FCSTD DOCUMENT
Label: gyuru_volume_alja_teljes
objects: Sketcher::SketchObject×1
note: 1 computed .brp shape members not serialized (recipe doc carries the construction recipe); baked Part::Feature solids carry a one-line shape summary decoded from their .brp

FEATURE [Sketcher::SketchObject] Sketch
  sketch-geometry (6):
    g0: LineSegment [constr] StartX=-6.61022 StartY=89.12 StartZ=0 EndX=84.3207 EndY=89.12 EndZ=0
    g1: LineSegment StartX=50 StartY=96.6176 StartZ=0 EndX=50 EndY=0 EndZ=0
    g2: ArcOfCircle CenterX=25 CenterY=152.92 CenterZ=0 NormalX=0 NormalY=0 NormalZ=1 Radius=63.8 StartAngle=4.34839 EndAngle=5.07639
    g3: ArcOfCircle CenterX=46.45 CenterY=96.6176 CenterZ=0 NormalX=0 NormalY=0 NormalZ=1 Radius=3.55 StartAngle=5.07639 EndAngle=6.28319
    g4: ArcOfCircle CenterX=3.55 CenterY=96.6176 CenterZ=0 NormalX=0 NormalY=0 NormalZ=1 Radius=3.55 StartAngle=3.14159 EndAngle=4.34839
    g5: LineSegment StartX=0 StartY=96.6176 StartZ=0 EndX=0 EndY=0 EndZ=0
  constraints (20):
    c: Horizontal(g0)
    c: DistanceY(g0) = 89.12
    c: Vertical(g1)
    c: DistanceX(g1) = 50
    c: Radius(g2) = 63.8
    c: Tangent(g2,g0)
    c: DistanceX(g2) = 25
    c: PointOnObject(g1,g-1)
    c: Radius(g3) = 3.55
    c: Radius(g4) = 3.55
    c: Tangent(g4,g2)
    c: Tangent(g3,g2)
    c: Tangent(g3,g1)
    c: Vertical(g5)
    c: Tangent(g5,g4)
    c: Tangent(g5,g4)
    c: DistanceX(g5) = 0
    c: Coincident(g3,g1)
    c: Coincident(g4,g5)
    c: PointOnObject(g5,g-1)
